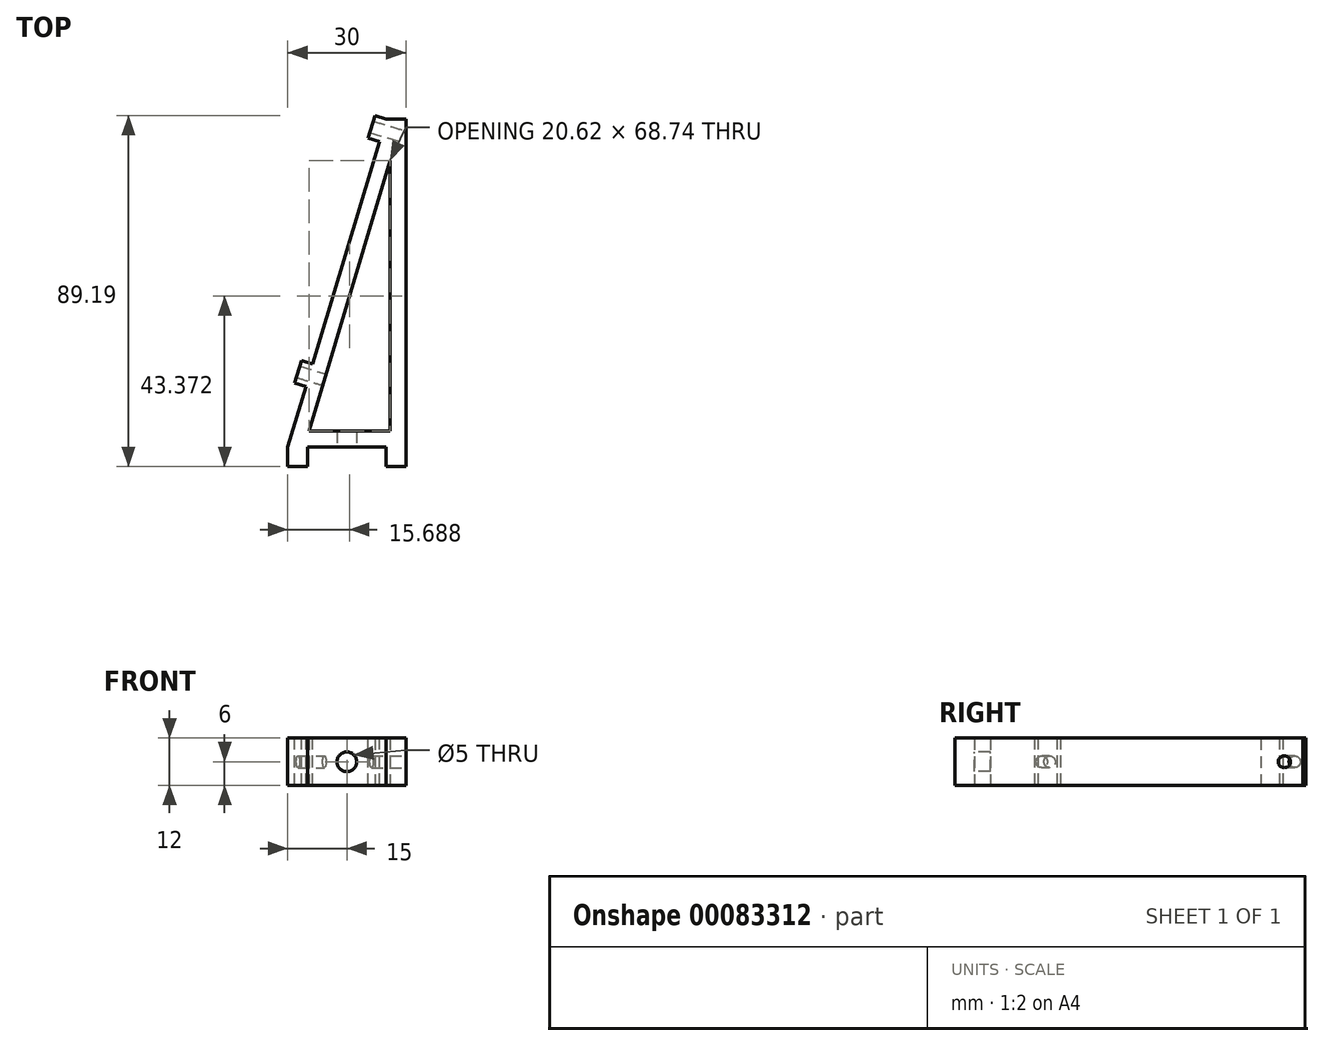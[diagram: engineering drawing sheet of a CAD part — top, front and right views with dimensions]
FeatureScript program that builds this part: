
annotation { "Feature Type Name" : "Feature", "Feature Type Description" : "" }
export const myFeature = defineFeature(function(context is Context, id is Id, definition is map)
    precondition{}
    {
        {
            var Q0;
            Q0=qCreatedBy(makeId("Top.planeOp"),FACE);
            var sketch = newSketch(context, id + "F0", { "sketchPlane" : qUnion([Q0])});
            skLineSegment(sketch, "E0", {"start": v(-20, 0) * mm, "end": v(0, 0) * mm});
            skLineSegment(sketch, "E1", {"start": v(0, 0) * mm, "end": v(0, -5) * mm});
            skLineSegment(sketch, "E2", {"start": v(0, -5) * mm, "end": v(5, -5) * mm});
            skLineSegment(sketch, "E3", {"start": v(5, -5) * mm, "end": v(5, 83.33) * mm});
            skLineSegment(sketch, "E4", {"start": v(-25, 0) * mm, "end": v(-25, -5) * mm});
            skLineSegment(sketch, "E5", {"start": v(-25, -5) * mm, "end": v(-20, -5) * mm});
            skLineSegment(sketch, "E6", {"start": v(-20, -5) * mm, "end": v(-20, 0) * mm});
            skLineSegment(sketch, "E7", {"start": v(5, 83.33) * mm, "end": v(0, 83.33) * mm});
            skLineSegment(sketch, "E8", {"start": v(0, 83.33) * mm, "end": v(-25, 0) * mm});
            skLineSegment(sketch, "E9", {"start": v(-19.62, 4) * mm, "end": v(1, 72.74) * mm});
            skLineSegment(sketch, "E10", {"start": v(1, 72.74) * mm, "end": v(1, 4) * mm});
            skLineSegment(sketch, "E11", {"start": v(1, 4) * mm, "end": v(-19.62, 4) * mm});
            skSolve(sketch);
        }
        {
            var Q0;
            Q0=qSketchRegion(id+"F0",true);
            extrude(context, id + "F1", {"entities" : qUnion([Q0]), "depth" : 12 * mm});
        }
        {
            var Q0;
            Q0=makeQuery(id+"F1.opExtrude","SWEPT_FACE",FACE,{"disambiguationData":[OSD([sQuery(id+"F0.wireOp",EDGE,"E0")])]});
            var sketch = newSketch(context, id + "F2", { "sketchPlane" : qUnion([Q0])});
            skCircle(sketch, "E12", {"center": v(-10, 6) * mm, "radius": 2.5 * mm});
            skSolve(sketch);
        }
        {
            var Q0;
            Q0=qSketchRegion(id+"F2",true);
            extrude(context, id + "F3", {"entities" : qUnion([Q0]), "operationType" : NewBodyOperationType.REMOVE, "endBound" : BoundingType.UP_TO_NEXT, "oppositeDirection" : true, "depth" : 25 * mm});
        }
        {
            var Q0;
            Q0=makeQuery(id+"F1.opExtrude","SWEPT_FACE",FACE,{"disambiguationData":[OSD([sQuery(id+"F0.wireOp",EDGE,"E8")])]});
            var sketch = newSketch(context, id + "F4", { "sketchPlane" : qUnion([Q0])});
            skLineSegment(sketch, "E13.bottom", {"start": v(-79.82, 0) * mm, "end": v(-73.82, 0) * mm});
            skLineSegment(sketch, "E13.top", {"start": v(-79.82, 12) * mm, "end": v(-73.82, 12) * mm});
            skLineSegment(sketch, "E13.left", {"start": v(-79.82, 0) * mm, "end": v(-79.82, 12) * mm});
            skLineSegment(sketch, "E13.right", {"start": v(-73.82, 0) * mm, "end": v(-73.82, 12) * mm});
            skLineSegment(sketch, "E14.bottom", {"start": v(-14.82, 0) * mm, "end": v(-8.82, 0) * mm});
            skLineSegment(sketch, "E14.top", {"start": v(-14.82, 12) * mm, "end": v(-8.82, 12) * mm});
            skLineSegment(sketch, "E14.left", {"start": v(-14.82, 0) * mm, "end": v(-14.82, 12) * mm});
            skLineSegment(sketch, "E14.right", {"start": v(-8.82, 0) * mm, "end": v(-8.82, 12) * mm});
            skCircle(sketch, "E15", {"center": v(-76.82, 6) * mm, "radius": 1.5 * mm});
            skCircle(sketch, "E16", {"center": v(-11.82, 6) * mm, "radius": 1.5 * mm});
            skPoint(sketch, "E16.centerSnap0", {"position": v(-8.82, 6) * mm});
            skSolve(sketch);
        }
        {
            var Q0;
            Q0=makeQuery(id+"F4.imprint","IMPRINT",FACE,{"disambiguationData":[TD([[makeQuery(id+"F4.imprint","IMPRINT",EDGE,{"derivedFrom":sQuery(id+"F4.wireOp",EDGE,"E13.bottom")}),1.0]])]});
            var Q1;
            Q1=makeQuery(id+"F4.imprint","IMPRINT",FACE,{"disambiguationData":[TD([[makeQuery(id+"F4.imprint","IMPRINT",EDGE,{"derivedFrom":sQuery(id+"F4.wireOp",EDGE,"E14.bottom")}),1.0]])]});
            extrude(context, id + "F5", {"entities" : qUnion([Q0, Q1]), "operationType" : NewBodyOperationType.ADD, "depth" : 3 * mm});
        }
        {
            var Q0;
            Q0=makeQuery(id+"F4.imprint","IMPRINT",FACE,{"disambiguationData":[TD([[makeQuery(id+"F4.imprint","IMPRINT",EDGE,{"derivedFrom":sQuery(id+"F4.wireOp",EDGE,"E15")}),1.0]])]});
            var Q1;
            Q1=makeQuery(id+"F4.imprint","IMPRINT",FACE,{"disambiguationData":[TD([[makeQuery(id+"F4.imprint","IMPRINT",EDGE,{"derivedFrom":sQuery(id+"F4.wireOp",EDGE,"E16")}),1.0]])]});
            extrude(context, id + "F6", {"entities" : qUnion([Q0, Q1]), "operationType" : NewBodyOperationType.REMOVE, "endBound" : BoundingType.UP_TO_NEXT, "oppositeDirection" : true, "depth" : 25 * mm});
        }
    });
